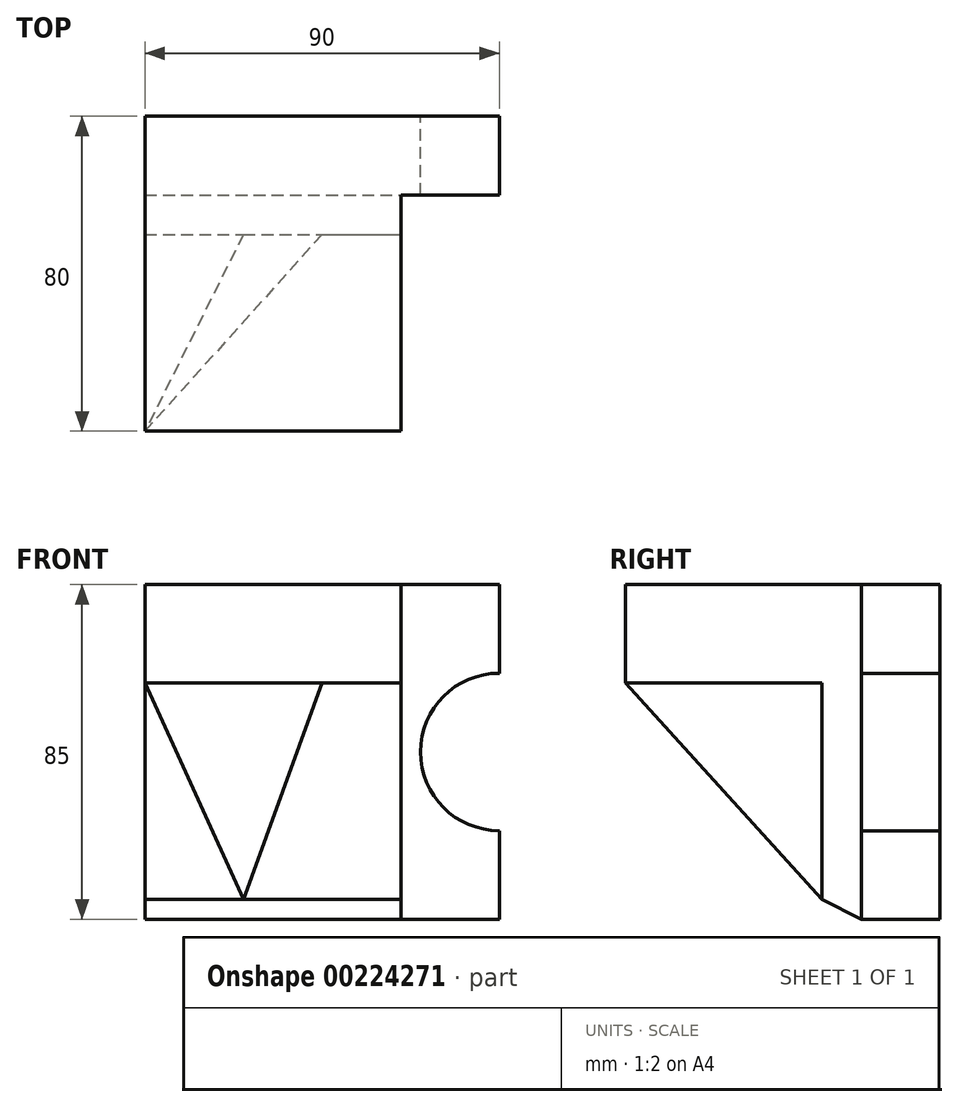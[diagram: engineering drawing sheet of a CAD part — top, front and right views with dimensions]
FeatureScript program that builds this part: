
annotation { "Feature Type Name" : "Feature", "Feature Type Description" : "" }
export const myFeature = defineFeature(function(context is Context, id is Id, definition is map)
    precondition{}
    {
        {
            var Q0;
            Q0=qCreatedBy(makeId("Front.planeOp"),FACE);
            var sketch = newSketch(context, id + "F0", { "sketchPlane" : qUnion([Q0])});
            skLineSegment(sketch, "E0.bottom", {"start": v(45, 42.5) * mm, "end": v(-45, 42.5) * mm});
            skLineSegment(sketch, "E0.top", {"start": v(45, -42.5) * mm, "end": v(-45, -42.5) * mm});
            skLineSegment(sketch, "E0.left", {"start": v(45, 42.5) * mm, "end": v(45, -42.5) * mm});
            skLineSegment(sketch, "E0.right", {"start": v(-45, 42.5) * mm, "end": v(-45, -42.5) * mm});
            skPoint(sketch, "E0.middle", {"position": v(0, 0) * mm});
            skSolve(sketch);
        }
        {
            var Q0;
            Q0 = qSketchRegion(id + "F0", true);
            extrude(context, id + "F1", {"entities" : qUnion([Q0]), "depth" : 20 * mm});
        }
        {
            var Q0;
            Q0=qCreatedBy(makeId("Front.planeOp"),FACE);
            var sketch = newSketch(context, id + "F2", { "sketchPlane" : qUnion([Q0])});
            skArc(sketch, "E1", {"start": v(45, 20) * mm, "mid": v(25, 0) * mm, "end": v(45, -20) * mm});
            skLineSegment(sketch, "E2.0", {"start": v(45, 42.5) * mm, "end": v(45, -42.5) * mm});
            skSolve(sketch);
        }
        {
            var Q0;
            {var subQ0=sQuery(id+"F2.wireOp",EDGE,"E1");Q0=makeQuery(id+"F2.imprint","IMPRINT",FACE,{"disambiguationData":[TD([[makeQuery(id+"F2.imprint","IMPRINT",EDGE,{"derivedFrom":subQ0}),1.0]])]});}
            extrude(context, id + "F3", {"entities" : qUnion([Q0]), "operationType" : NewBodyOperationType.REMOVE, "depth" : 25 * mm});
        }
        {
            var Q0;
            {var subQ0=sQuery(id+"F0.wireOp",EDGE,"E0.bottom");var subQ2=sQuery(id+"F0.wireOp",EDGE,"E0.left");Q0=makeQuery(id+"F3.boolean.opBoolean","SPLIT",FACE,{"disambiguationData":[TD([makeQuery(id+"F1.opExtrude","SWEPT_FACE",FACE,{"disambiguationData":[OSD([subQ0])]})])],"derivedFrom":makeQuery(id+"F1.opExtrude","SWEPT_FACE",FACE,{"disambiguationData":[OSD([subQ2])]})});}
            cPlane(context, id + "F4", {"entities" : qUnion([Q0]), "cplaneType" : CPlaneType.OFFSET, "offset" : 25 * mm, "oppositeDirection" : true, "width" : 150 * mm, "height" : 150 * mm});
        }
        {
            var Q0;
            Q0=qCreatedBy(id+"F4.planeOp",FACE);
            var sketch = newSketch(context, id + "F5", { "sketchPlane" : qUnion([Q0])});
            skLineSegment(sketch, "E3", {"start": v(-20, 42.5) * mm, "end": v(-80, 42.5) * mm});
            skLineSegment(sketch, "E4", {"start": v(-80, 42.5) * mm, "end": v(-80, 17.5) * mm});
            skLineSegment(sketch, "E5", {"start": v(-80, 17.5) * mm, "end": v(-30, 17.5) * mm});
            skLineSegment(sketch, "E6", {"start": v(-30, 17.5) * mm, "end": v(-30, -37.5) * mm});
            skLineSegment(sketch, "E7", {"start": v(-30, -37.5) * mm, "end": v(-20, -42.5) * mm});
            skPoint(sketch, "E8.0", {"position": v(-20, -31.25) * mm});
            skLineSegment(sketch, "E9.0", {"start": v(-20, 20) * mm, "end": v(-20, -20) * mm});
            skLineSegment(sketch, "E10.0.0", {"start": v(-20, 42.5) * mm, "end": v(-20, 20) * mm});
            skLineSegment(sketch, "E10.0.1", {"start": v(-20, 20) * mm, "end": v(0, 20) * mm});
            skLineSegment(sketch, "E10.0.2", {"start": v(0, 20) * mm, "end": v(0, 42.5) * mm});
            skLineSegment(sketch, "E10.0.3", {"start": v(0, 42.5) * mm, "end": v(-20, 42.5) * mm});
            skLineSegment(sketch, "E11", {"start": v(-20, -42.5) * mm, "end": v(-20, 42.5) * mm});
            skSolve(sketch);
        }
        {
            var Q0;
            {var subQ1=sQuery(id+"F5.wireOp",EDGE,"E3");Q0=makeQuery(id+"F5.imprint","IMPRINT",FACE,{"disambiguationData":[TD([[makeQuery(id+"F5.imprint","IMPRINT",EDGE,{"derivedFrom":subQ1}),1.0]])]});}
            extrude(context, id + "F6", {"entities" : qUnion([Q0]), "operationType" : NewBodyOperationType.ADD, "oppositeDirection" : true, "depth" : 65 * mm});
        }
        {
            var Q0;
            Q0=makeQuery(id+"F6.opExtrude","SWEPT_FACE",FACE,{"disambiguationData":[OSD([sQuery(id+"F5.wireOp",EDGE,"E6")])]});
            var sketch = newSketch(context, id + "F7", { "sketchPlane" : qUnion([Q0])});
            skPoint(sketch, "E12", {"position": v(0, 17.5) * mm});
            skPoint(sketch, "E13", {"position": v(-20, -37.5) * mm});
            skSolve(sketch);
        }
        {
            var Q0;
            {var subQ0=sQuery(id+"F5.wireOp",EDGE,"E6");Q0=makeQuery(id+"F7.imprint","IMPRINT",FACE,{"disambiguationData":[TD([[makeQuery(id+"F7.imprint","IMPRINT",EDGE,{"derivedFrom":makeQuery(id+"F6.opExtrude","CAP_EDGE",EDGE,{"disambiguationData":[OSD([subQ0])],"isStart":true})}),-1.0]])]});}
            var sketch = newSketch(context, id + "F8", { "sketchPlane" : qUnion([Q0])});
            skLineSegment(sketch, "E14", {"start": v(-20, -37.5) * mm, "end": v(0, 17.5) * mm});
            skLineSegment(sketch, "E15.0", {"start": v(-45, -37.5) * mm, "end": v(-20, -37.5) * mm});
            skPoint(sketch, "E16.orphan", {"position": v(20, -37.5) * mm});
            skLineSegment(sketch, "E17.0", {"start": v(-45, 17.5) * mm, "end": v(-45, -37.5) * mm});
            skLineSegment(sketch, "E18.0", {"start": v(-45, 17.5) * mm, "end": v(0, 17.5) * mm});
            skPoint(sketch, "E19.orphan", {"position": v(20, 17.5) * mm});
            skSolve(sketch);
        }
        {
            var Q0;
            Q0=makeQuery(id+"F6.opExtrude","SWEPT_FACE",FACE,{"disambiguationData":[OSD([sQuery(id+"F5.wireOp",EDGE,"E4")])]});
            var sketch = newSketch(context, id + "F9", { "sketchPlane" : qUnion([Q0])});
            skPoint(sketch, "E20", {"position": v(-45, 17.5) * mm});
            skSolve(sketch);
        }
        {
            var Q1;
            Q1=makeQuery(id+"F8.imprint","IMPRINT",FACE,{"disambiguationData":[TD([[makeQuery(id+"F8.imprint","IMPRINT",EDGE,{"derivedFrom":sQuery(id+"F8.wireOp",EDGE,"E14")}),1.0]])]});
            var Q2;
            Q2=sQuery(id+"F9.wireOp",VERTEX,"E20");
            loft(context, id + "F10", {"operationType" : NewBodyOperationType.ADD, "sheetProfilesArray" : [{ "sheetProfileEntities" : qUnion([Q1]) }, { "sheetProfileEntities" : qUnion([Q2]) }]});
        }
    });
